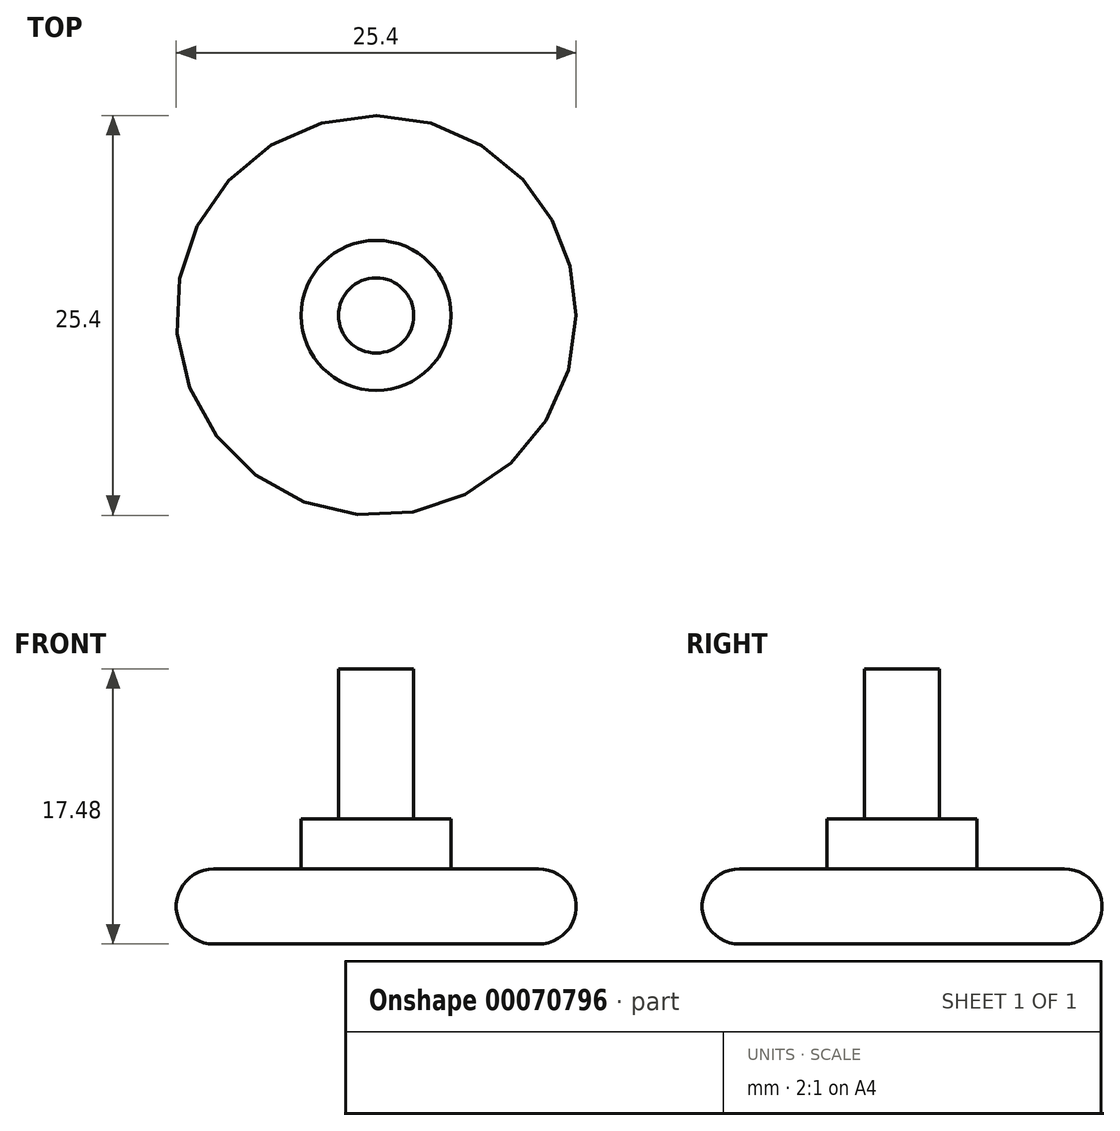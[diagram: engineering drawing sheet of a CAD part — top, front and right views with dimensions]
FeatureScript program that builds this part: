
annotation { "Feature Type Name" : "Feature", "Feature Type Description" : "" }
export const myFeature = defineFeature(function(context is Context, id is Id, definition is map)
    precondition{}
    {
        {
            var Q0;
            Q0=qCreatedBy(makeId("Front.planeOp"),FACE);
            var sketch = newSketch(context, id + "F0", { "sketchPlane" : qUnion([Q0])});
            skLineSegment(sketch, "E0.bottom", {"start": v(0, 0) * mm, "end": v(-12.7, 0) * mm});
            skLineSegment(sketch, "E0.top", {"start": v(0, 4.78) * mm, "end": v(-12.7, 4.78) * mm});
            skLineSegment(sketch, "E0.left", {"start": v(0, 0) * mm, "end": v(0, 4.78) * mm});
            skLineSegment(sketch, "E0.right", {"start": v(-12.7, 0) * mm, "end": v(-12.7, 4.78) * mm});
            skSolve(sketch);
        }
        {
            var Q0;
            Q0=makeQuery(id+"F0.imprint","IMPRINT",FACE,{"disambiguationData":[TD([[makeQuery(id+"F0.imprint","IMPRINT",EDGE,{"derivedFrom":sQuery(id+"F0.wireOp",EDGE,"E0.bottom")}),-1.0]])]});
            var Q1;
            Q1=sQuery(id+"F0.wireOp",EDGE,"E0.right");
            revolve(context, id + "F1", {"entities" : qUnion([Q0]), "axis" : qUnion([Q1]), "revolveType" : RevolveType.FULL});
        }
        {
            var Q0;
            Q0=makeQuery(id+"F1.opRevolve","SWEPT_FACE",FACE,{"disambiguationData":[OSD([sQuery(id+"F0.wireOp",EDGE,"E0.left")])]});
            var Q1;
            Q1=makeQuery(id+"F1.opRevolve","SWEPT_FACE",FACE,{"disambiguationData":[OSD([sQuery(id+"F0.wireOp",EDGE,"E0.top")])]});
            var Q2;
            Q2=makeQuery(id+"F1.opRevolve","SWEPT_FACE",FACE,{"disambiguationData":[OSD([sQuery(id+"F0.wireOp",EDGE,"E0.bottom")])]});
            fillet(context, id + "F2", {"entities" : qUnion([Q0, Q1, Q2]), "radius" : 2.4 * mm, "tangentPropagation" : true, "allowEdgeOverflow" : false});
        }
        {
            var Q0;
            Q0=makeQuery(id+"F1.opRevolve","SWEPT_FACE",FACE,{"disambiguationData":[OSD([sQuery(id+"F0.wireOp",EDGE,"E0.top")])]});
            var sketch = newSketch(context, id + "F3", { "sketchPlane" : qUnion([Q0])});
            skCircle(sketch, "E1", {"center": v(-12.7, 0) * mm, "radius": 4.76 * mm});
            skSolve(sketch);
        }
        {
            var Q0;
            Q0=makeQuery(id+"F3.imprint","IMPRINT",FACE,{"disambiguationData":[TD([[makeQuery(id+"F3.imprint","IMPRINT",EDGE,{"derivedFrom":sQuery(id+"F3.wireOp",EDGE,"E1")}),1.0]])]});
            extrude(context, id + "F4", {"entities" : qUnion([Q0]), "operationType" : NewBodyOperationType.ADD, "depth" : 3.17 * mm});
        }
        {
            var Q0;
            Q0=makeQuery(id+"F4.opExtrude","CAP_FACE",FACE,{"disambiguationData":[OSD([sQuery(id+"F3.wireOp",EDGE,"E1")])],"isStart":false});
            var sketch = newSketch(context, id + "F5", { "sketchPlane" : qUnion([Q0])});
            skCircle(sketch, "E2", {"center": v(-12.7, 0) * mm, "radius": 2.39 * mm});
            skSolve(sketch);
        }
        {
            var Q0;
            Q0=makeQuery(id+"F5.imprint","IMPRINT",FACE,{"disambiguationData":[TD([[makeQuery(id+"F5.imprint","IMPRINT",EDGE,{"derivedFrom":sQuery(id+"F5.wireOp",EDGE,"E2")}),1.0]])]});
            extrude(context, id + "F6", {"entities" : qUnion([Q0]), "operationType" : NewBodyOperationType.ADD, "depth" : 9.52 * mm});
        }
    });
